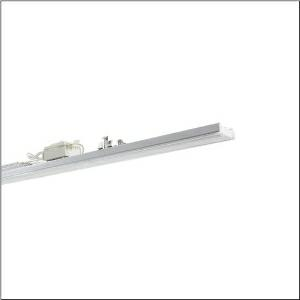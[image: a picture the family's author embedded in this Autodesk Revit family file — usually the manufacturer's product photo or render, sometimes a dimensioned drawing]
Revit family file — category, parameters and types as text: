
# Revit family: licross_21_recessed_mo_52te12dn4axg3c
name_source: partatom
category: Lighting Fixtures
units: mm (PartAtom-declared; Revit-internal decimal feet)

## family parameters
Cut with Voids When Loaded = No
Host = Face
Light Source = No
Part Type = Normal
Room Calculation Point = No
Round Connector Dimension = Use Diameter
Shared = No

## types (1)
- --- (1 x LED, 950 lm, 6.7 W, 4000K)
    Apparent Load = 7 VA
    CIE Flux Codes = 72 92 99 100 100
    Color Rendering = 80
    Color Temperature = 4000K
    Default Elevation = 1800 mm
    Description = Licross 21 Recessed MO, luminaire insert, of sheet steel, galvanised, coil coated, white, length: 1.500mm, width: 66mm, height: 67mm, LED rated luminous flux: 10.280lm, light colour: 840, SDCM (Standard Deviation of Colour Matching)MacAdam ≤ 3 SDCM (initial), control gear: DALI 2 (for two DALI lines), with plug, 6-pole, with phase selection, for trunking rail, 14-core, mains connection: 220..240V, AC, 50/60Hz, rated input power: 62W, internal wiring halogen-free, for emergency light function, for trunking rail, 14-core, converter,control gear: single battery element, battery: LiFePO4, 9Ah, primary optical cover: cover, of PMMA, light emission: direct distribution, primary light characteristic: symmetric, protection rating (complete): IP54, insulation class (complete): insulation class I (protective earthing), certification: CE, UKCA, protection symbol: D if used in an environment with non-conductive dust loads with corresponding accessories, impact resistance: IK06, permissible ambient temperature for indoor applications: +5..+35°C, standard: EN 60598-2-22, LABS conformity tested according to VDMA 24364:2018-05, reducing of maximum allowable ambient temperature of 5°C with ceiling mounting, corresponds to IFS (International Featured Standards) requirements for safety and quality in the food industry, The light source and the operating device comply with the requirements of the Ecodesign Regulation (EU) 2019/2020 and are replaceable in accordance with this regulation, packaging unit: 1 piece
    Height = 58 mm
    Lamp = 1 x LED
    Lamp Light Flux = 950 lm
    Lamp Power = 6.7 W
    Lamp count = 1
    Length = 1500 mm
    Luminous efficacy = 142 lm/W
    Manufacturer = Siteco
    ModVariant = No
    Model = 52TE12DN4AXG3C
    Mounting Place = Ceiling
    Mounting Type = Pendant
    Number of Poles = 1
    OnlyDefault = Yes
    Power Factor = 1
    Product Name = Licross 21 Recessed MO
    Product group = luminaire insert | ceiling pendant
    ProductGroupID = 901
    Protection Class = Protection class I
    Protection Degree = IP 54
    RLX_Detail_Level = 1
    RLX_Emergency_Light_Flux = 0 lm
    RLX_Emergency_Type = 0
    RLX_Emergency_Type_DB = No
    RlxData = <blob elided: 25329 chars, md5=a5ce9c13>
    Socket = socket
    Standby Power = 0 W
    System Light Flux = 950 lm
    System Power = 7 W
    Type Comments = : emergency light operation: 3 h
    Type Image = l_1296930.jpg
    URL = http://relux.com
    VarID = @adj_110001
    Voltage = 0 V
    Weight = 0.00 kg
    Width = 66 mm

## geometry (parser evidence)
native form markers: Blend x4, Sweep x13
no freeform markers — native parametric forms only
